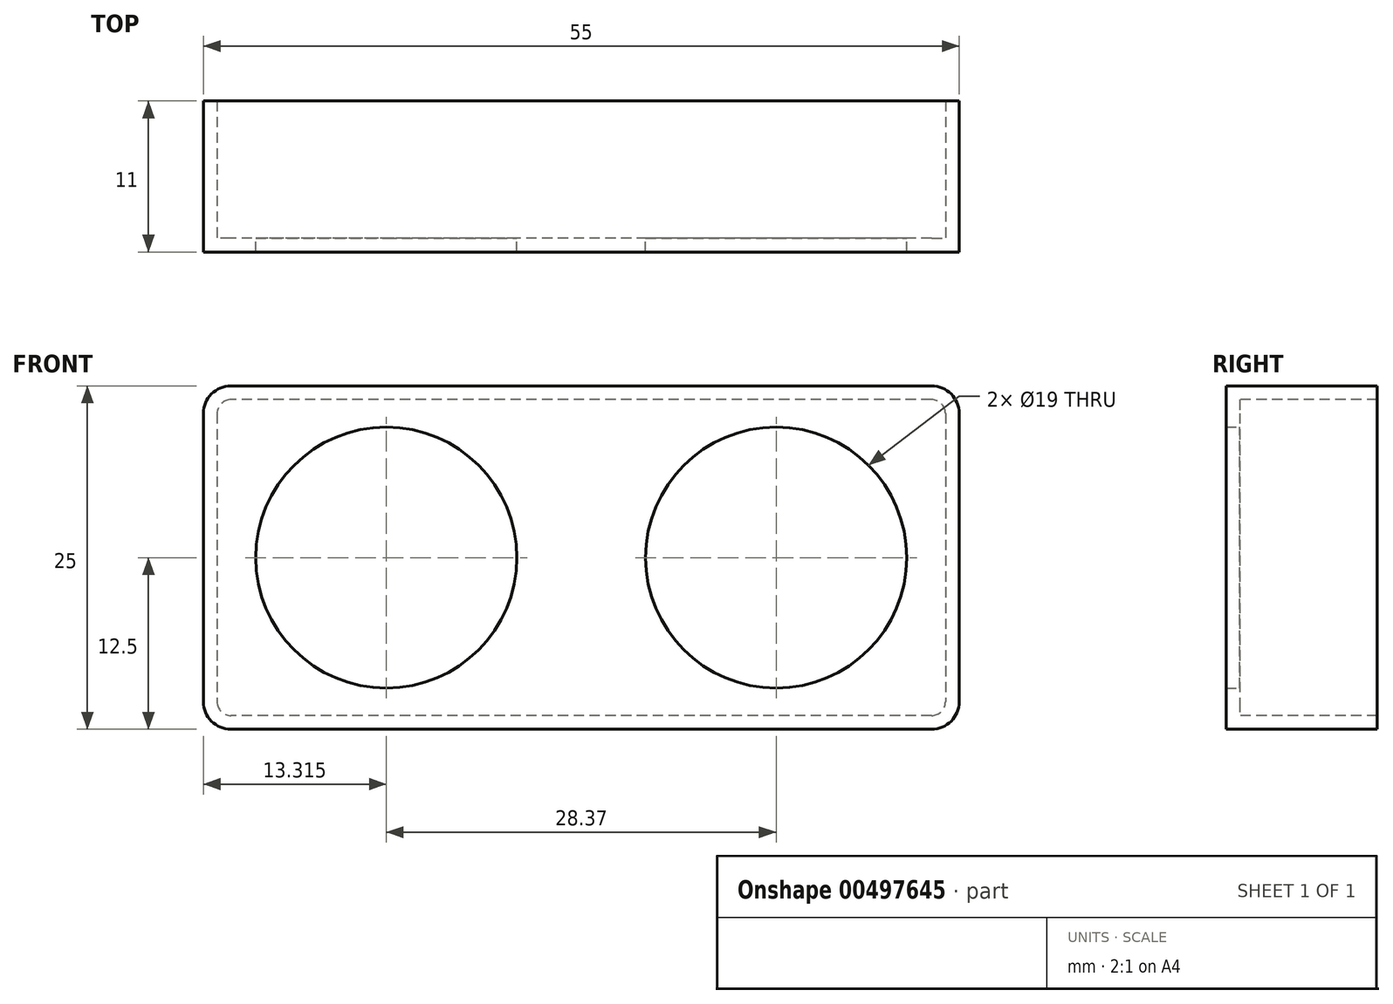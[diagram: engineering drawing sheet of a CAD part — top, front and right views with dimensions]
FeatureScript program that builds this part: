
annotation { "Feature Type Name" : "Feature", "Feature Type Description" : "" }
export const myFeature = defineFeature(function(context is Context, id is Id, definition is map)
    precondition{}
    {
        {
            var Q0;
            Q0=qCreatedBy(makeId("Front.planeOp"),FACE);
            var sketch = newSketch(context, id + "F0", { "sketchPlane" : qUnion([Q0])});
            skLineSegment(sketch, "E0.bottom", {"start": v(-25.5, 12.5) * mm, "end": v(25.5, 12.5) * mm});
            skLineSegment(sketch, "E0.top", {"start": v(-25.5, -12.5) * mm, "end": v(25.5, -12.5) * mm});
            skLineSegment(sketch, "E0.left", {"start": v(-27.5, 10.5) * mm, "end": v(-27.5, -10.5) * mm});
            skLineSegment(sketch, "E0.right", {"start": v(27.5, 10.5) * mm, "end": v(27.5, -10.5) * mm});
            skPoint(sketch, "E1.visualSharp", {"position": v(-27.5, 12.5) * mm});
            skArc(sketch, "E1.filletArc", {"start": v(-25.5, 12.5) * mm, "mid": v(-26.91, 11.91) * mm, "end": v(-27.5, 10.5) * mm});
            skPoint(sketch, "E2.visualSharp", {"position": v(27.5, 12.5) * mm});
            skArc(sketch, "E2.filletArc", {"start": v(27.5, 10.5) * mm, "mid": v(26.91, 11.91) * mm, "end": v(25.5, 12.5) * mm});
            skPoint(sketch, "E3.visualSharp", {"position": v(27.5, -12.5) * mm});
            skArc(sketch, "E3.filletArc", {"start": v(25.5, -12.5) * mm, "mid": v(26.91, -11.91) * mm, "end": v(27.5, -10.5) * mm});
            skPoint(sketch, "E4.visualSharp", {"position": v(-27.5, -12.5) * mm});
            skArc(sketch, "E4.filletArc", {"start": v(-27.5, -10.5) * mm, "mid": v(-26.91, -11.91) * mm, "end": v(-25.5, -12.5) * mm});
            skCircle(sketch, "E5", {"center": v(-14.18, 0) * mm, "radius": 9.5 * mm});
            skCircle(sketch, "E6", {"center": v(14.18, 0) * mm, "radius": 9.5 * mm});
            skSolve(sketch);
        }
        {
            var Q0;
            Q0=makeQuery(id+"F0.imprint","IMPRINT",FACE,{"disambiguationData":[TD([[makeQuery(id+"F0.imprint","IMPRINT",EDGE,{"derivedFrom":sQuery(id+"F0.wireOp",EDGE,"E0.bottom")}),-1.0]])]});
            extrude(context, id + "F1", {"entities" : qUnion([Q0]), "depth" : 1 * mm});
        }
        {
            var Q0;
            Q0=qCreatedBy(makeId("Front.planeOp"),FACE);
            var sketch = newSketch(context, id + "F2", { "sketchPlane" : qUnion([Q0])});
            skLineSegment(sketch, "E7.bottom", {"start": v(25.5, 11.5) * mm, "end": v(-25.5, 11.5) * mm});
            skLineSegment(sketch, "E7.top", {"start": v(25.5, -11.5) * mm, "end": v(-25.5, -11.5) * mm});
            skLineSegment(sketch, "E7.left", {"start": v(26.5, 10.5) * mm, "end": v(26.5, -10.5) * mm});
            skLineSegment(sketch, "E7.right", {"start": v(-26.5, 10.5) * mm, "end": v(-26.5, -10.5) * mm});
            skPoint(sketch, "E8.visualSharp", {"position": v(26.5, 11.5) * mm});
            skArc(sketch, "E8.filletArc", {"start": v(26.5, 10.5) * mm, "mid": v(26.2, 11.2) * mm, "end": v(25.5, 11.5) * mm});
            skPoint(sketch, "E9.visualSharp", {"position": v(-26.5, 11.5) * mm});
            skArc(sketch, "E9.filletArc", {"start": v(-25.5, 11.5) * mm, "mid": v(-26.2, 11.2) * mm, "end": v(-26.5, 10.5) * mm});
            skPoint(sketch, "E10.visualSharp", {"position": v(-26.5, -11.5) * mm});
            skArc(sketch, "E10.filletArc", {"start": v(-26.5, -10.5) * mm, "mid": v(-26.2, -11.2) * mm, "end": v(-25.5, -11.5) * mm});
            skPoint(sketch, "E11.visualSharp", {"position": v(26.5, -11.5) * mm});
            skArc(sketch, "E11.filletArc", {"start": v(25.5, -11.5) * mm, "mid": v(26.2, -11.2) * mm, "end": v(26.5, -10.5) * mm});
            skSolve(sketch);
        }
        {
            var Q0;
            Q0 = qSketchRegion(id + "F0", true);
            extrude(context, id + "F3", {"entities" : qUnion([Q0]), "operationType" : NewBodyOperationType.ADD, "oppositeDirection" : true, "depth" : 10 * mm});
        }
        {
            var Q0;
            Q0 = qSketchRegion(id + "F2", true);
            extrude(context, id + "F4", {"entities" : qUnion([Q0]), "operationType" : NewBodyOperationType.REMOVE, "oppositeDirection" : true, "depth" : 35.9 * mm});
        }
    });
